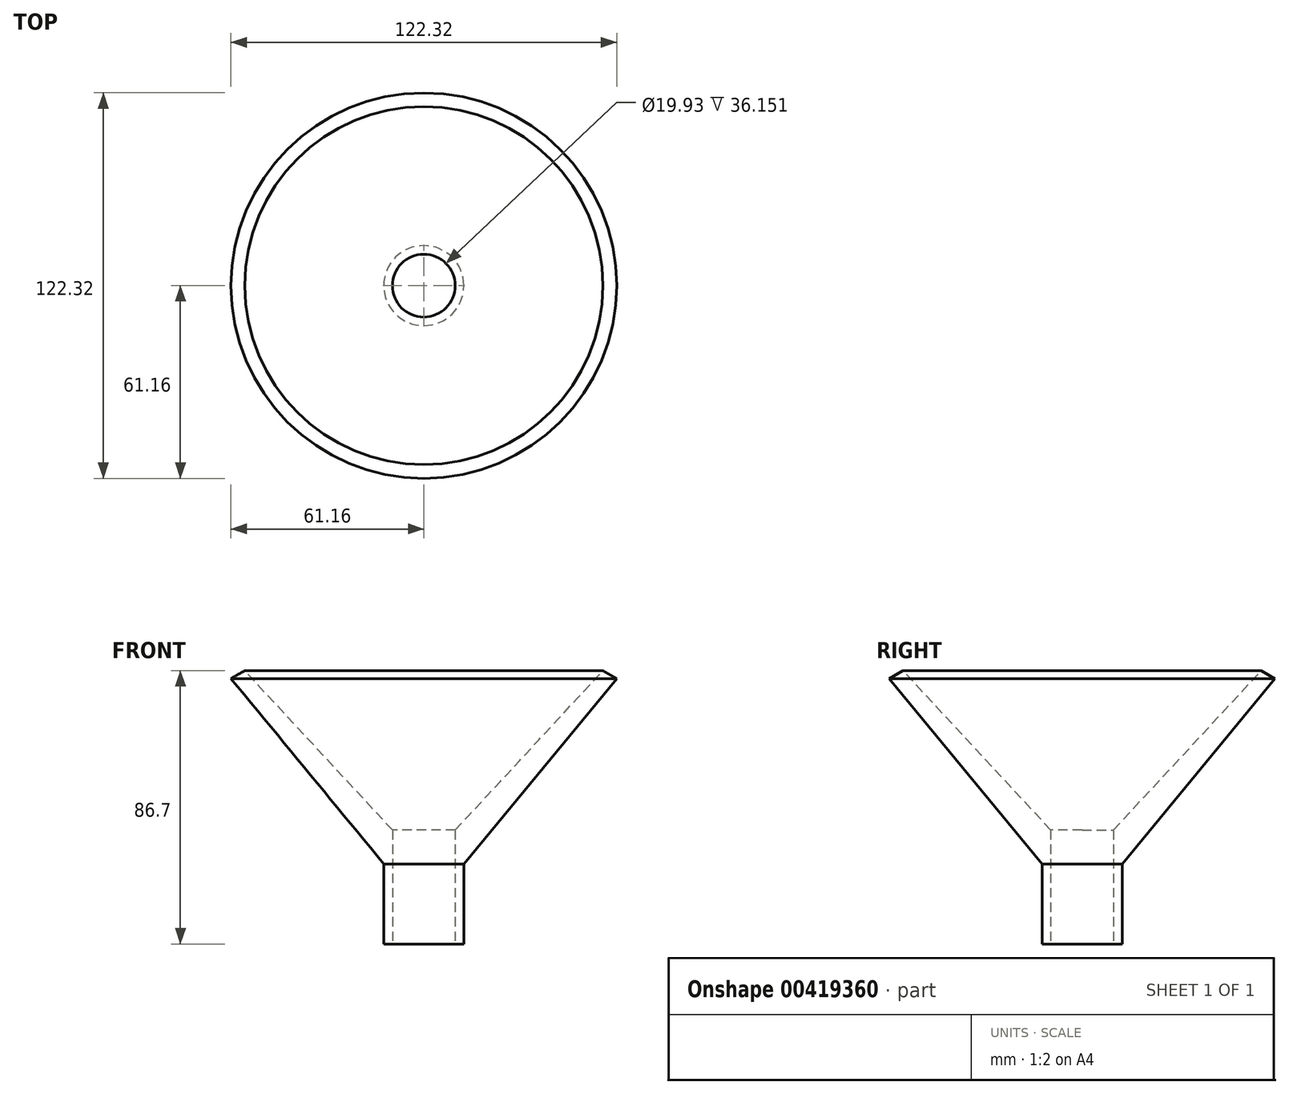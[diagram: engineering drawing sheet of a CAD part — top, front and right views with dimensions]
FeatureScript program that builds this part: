
annotation { "Feature Type Name" : "Feature", "Feature Type Description" : "" }
export const myFeature = defineFeature(function(context is Context, id is Id, definition is map)
    precondition{}
    {
        {
            var Q0;
            Q0=qCreatedBy(makeId("Front.planeOp"),FACE);
            var sketch = newSketch(context, id + "F0", { "sketchPlane" : qUnion([Q0])});
            skLineSegment(sketch, "E0", {"start": v(48.46, 58.8) * mm, "end": v(0, 0) * mm});
            skLineSegment(sketch, "E1", {"start": v(0, 0) * mm, "end": v(0, -25.4) * mm});
            skLineSegment(sketch, "E2", {"start": v(0, -25.4) * mm, "end": v(-12.7, -25.4) * mm});
            skLineSegment(sketch, "E3", {"start": v(-12.7, -25.4) * mm, "end": v(-12.7, 0) * mm});
            skLineSegment(sketch, "E4", {"start": v(-12.7, 0) * mm, "end": v(44.11, 61.3) * mm});
            skLineSegment(sketch, "E5", {"start": v(44.11, 61.3) * mm, "end": v(48.46, 58.8) * mm});
            skSolve(sketch);
        }
        {
            var Q0;
            Q0=makeQuery(id+"F0.imprint","IMPRINT",FACE,{"disambiguationData":[TD([[makeQuery(id+"F0.imprint","IMPRINT",EDGE,{"derivedFrom":sQuery(id+"F0.wireOp",EDGE,"E0")}),-1.0]])]});
            var Q1;
            Q1=sQuery(id+"F0.wireOp",EDGE,"E3");
            revolve(context, id + "F1", {"entities" : qUnion([Q0]), "axis" : qUnion([Q1]), "revolveType" : RevolveType.FULL});
        }
        {
            var Q0;
            Q0=makeQuery(id+"F1.opRevolve","SWEPT_FACE",FACE,{"disambiguationData":[OSD([sQuery(id+"F0.wireOp",EDGE,"E2")])]});
            var sketch = newSketch(context, id + "F2", { "sketchPlane" : qUnion([Q0])});
            skCircle(sketch, "E6", {"center": v(-12.7, 0) * mm, "radius": 9.96 * mm});
            skSolve(sketch);
        }
        {
            var Q0;
            Q0=makeQuery(id+"F2.imprint","IMPRINT",FACE,{"disambiguationData":[TD([[makeQuery(id+"F2.imprint","IMPRINT",EDGE,{"derivedFrom":sQuery(id+"F2.wireOp",EDGE,"E6")}),1.0]])]});
            extrude(context, id + "F3", {"entities" : qUnion([Q0]), "operationType" : NewBodyOperationType.REMOVE, "oppositeDirection" : true, "depth" : 50.8 * mm});
        }
    });
